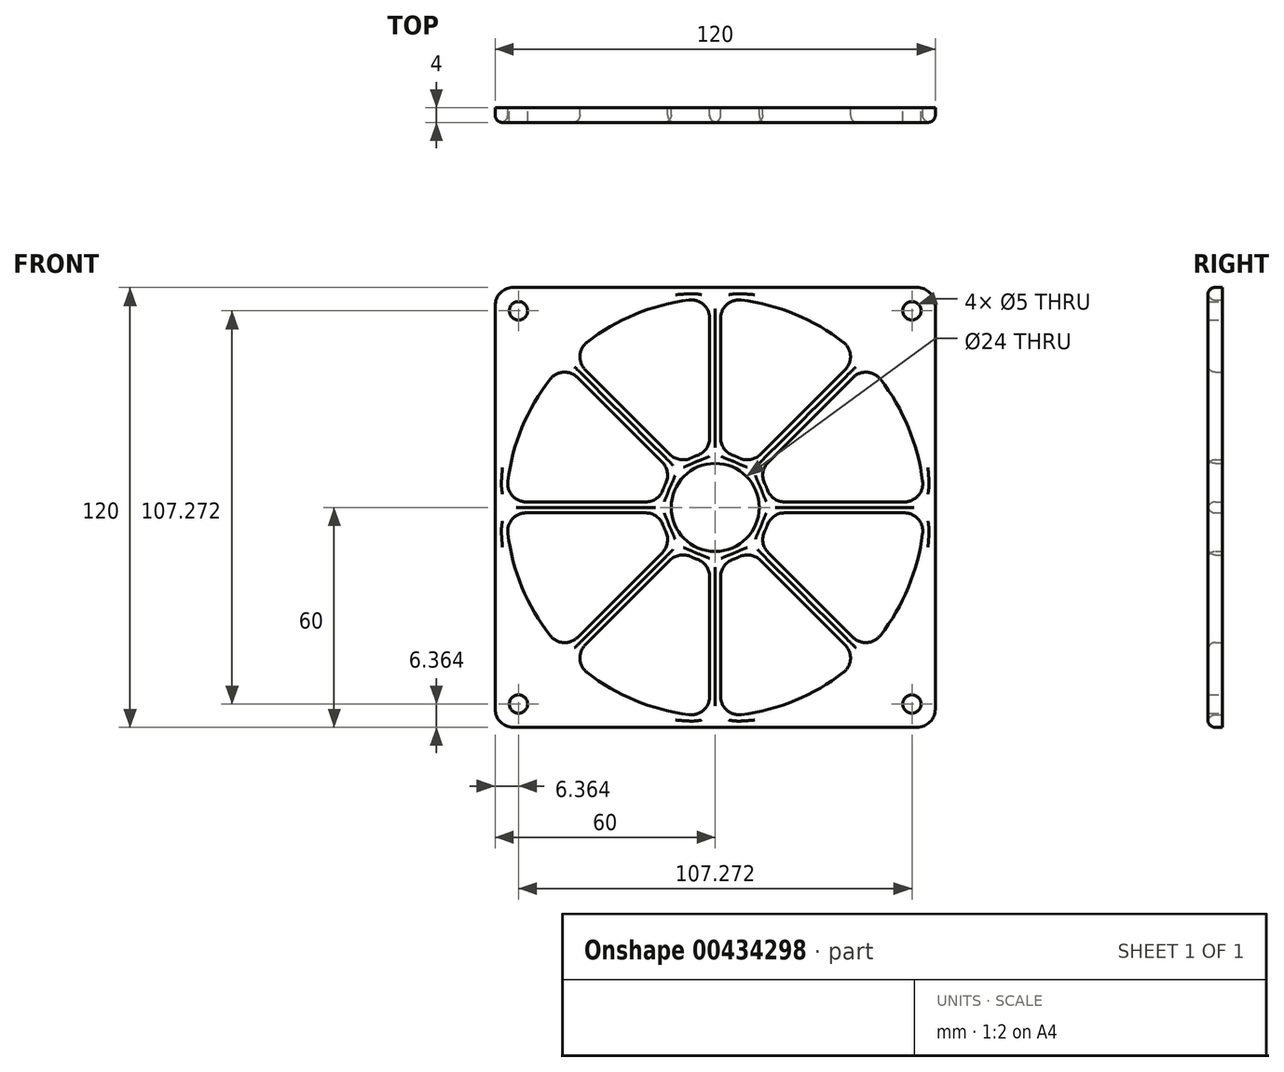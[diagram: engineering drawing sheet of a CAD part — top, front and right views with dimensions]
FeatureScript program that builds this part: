
annotation { "Feature Type Name" : "Feature", "Feature Type Description" : "" }
export const myFeature = defineFeature(function(context is Context, id is Id, definition is map)
    precondition{}
    {
        {
            var Q0;
            Q0=qCreatedBy(makeId("Front.planeOp"),FACE);
            var sketch = newSketch(context, id + "F0", { "sketchPlane" : qUnion([Q0])});
            skLineSegment(sketch, "E0.bottom", {"start": v(-60, 60) * mm, "end": v(60, 60) * mm});
            skLineSegment(sketch, "E0.top", {"start": v(-60, -60) * mm, "end": v(60, -60) * mm});
            skLineSegment(sketch, "E0.left", {"start": v(-60, 60) * mm, "end": v(-60, -60) * mm});
            skLineSegment(sketch, "E0.right", {"start": v(60, 60) * mm, "end": v(60, -60) * mm});
            skCircle(sketch, "E1", {"center": v(0, 0) * mm, "radius": 57 * mm});
            skCircle(sketch, "E2", {"center": v(0, 0) * mm, "radius": 15 * mm});
            skLineSegment(sketch, "E3", {"start": v(0, 57) * mm, "end": v(0, 15) * mm});
            skLineSegment(sketch, "E4", {"start": v(15, 0) * mm, "end": v(57, 0) * mm});
            skLineSegment(sketch, "E5", {"start": v(0, -15) * mm, "end": v(0, -57) * mm});
            skLineSegment(sketch, "E6", {"start": v(-15, 0) * mm, "end": v(-57, 0) * mm});
            skLineSegment(sketch, "E7", {"start": v(-1.5, -14.92) * mm, "end": v(-1.5, -56.98) * mm});
            skLineSegment(sketch, "E8", {"start": v(1.5, -14.92) * mm, "end": v(1.5, -56.98) * mm});
            skLineSegment(sketch, "E9", {"start": v(9.5, -11.61) * mm, "end": v(39.23, -41.35) * mm});
            skLineSegment(sketch, "E10", {"start": v(11.61, -9.5) * mm, "end": v(41.35, -39.23) * mm});
            skLineSegment(sketch, "E11", {"start": v(14.92, -1.5) * mm, "end": v(56.98, -1.5) * mm});
            skLineSegment(sketch, "E12", {"start": v(14.92, 1.5) * mm, "end": v(56.98, 1.5) * mm});
            skLineSegment(sketch, "E13", {"start": v(11.61, 9.5) * mm, "end": v(41.35, 39.23) * mm});
            skLineSegment(sketch, "E14", {"start": v(9.5, 11.61) * mm, "end": v(39.23, 41.35) * mm});
            skLineSegment(sketch, "E15", {"start": v(1.5, 14.93) * mm, "end": v(1.5, 56.98) * mm});
            skLineSegment(sketch, "E16", {"start": v(-1.5, 56.98) * mm, "end": v(-1.5, 14.92) * mm});
            skLineSegment(sketch, "E17", {"start": v(-9.5, 11.61) * mm, "end": v(-39.23, 41.35) * mm});
            skLineSegment(sketch, "E18", {"start": v(-11.61, 9.5) * mm, "end": v(-41.35, 39.23) * mm});
            skLineSegment(sketch, "E19", {"start": v(-14.92, 1.5) * mm, "end": v(-56.98, 1.5) * mm});
            skLineSegment(sketch, "E20", {"start": v(-14.93, -1.5) * mm, "end": v(-56.98, -1.5) * mm});
            skLineSegment(sketch, "E21", {"start": v(-9.5, -11.61) * mm, "end": v(-39.23, -41.35) * mm});
            skLineSegment(sketch, "E22", {"start": v(-11.61, -9.5) * mm, "end": v(-41.35, -39.23) * mm});
            skPoint(sketch, "E23", {"position": v(40.3, -40.3) * mm});
            skPoint(sketch, "E24", {"position": v(40.3, 40.3) * mm});
            skPoint(sketch, "E25", {"position": v(-40.3, 40.3) * mm});
            skPoint(sketch, "E26", {"position": v(-10.6, 10.6) * mm});
            skPoint(sketch, "E27", {"position": v(10.6, 10.6) * mm});
            skPoint(sketch, "E28", {"position": v(-10.6, -10.6) * mm});
            skPoint(sketch, "E29", {"position": v(10.6, -10.6) * mm});
            skPoint(sketch, "E30", {"position": v(-40.3, -40.3) * mm});
            skCircle(sketch, "E31", {"center": v(-53.64, -53.64) * mm, "radius": 2.5 * mm});
            skCircle(sketch, "E32", {"center": v(53.64, -53.64) * mm, "radius": 2.5 * mm});
            skCircle(sketch, "E33", {"center": v(53.64, 53.64) * mm, "radius": 2.5 * mm});
            skCircle(sketch, "E34", {"center": v(-53.64, 53.64) * mm, "radius": 2.5 * mm});
            skCircle(sketch, "E35", {"center": v(0, 0) * mm, "radius": 12 * mm});
            skSolve(sketch);
        }
        {
            var Q0;
            Q0=makeQuery(id+"F0.imprint","IMPRINT",FACE,{"disambiguationData":[TD([[makeQuery(id+"F0.imprint","IMPRINT",EDGE,{"derivedFrom":sQuery(id+"F0.wireOp",EDGE,"E0.bottom")}),-1.0]])]});
            var Q1;
            {var subQ0=sQuery(id+"F0.wireOp",EDGE,"E17");Q1=makeQuery(id+"F0.imprint","IMPRINT",FACE,{"disambiguationData":[TD([[makeQuery(id+"F0.imprint","IMPRINT",EDGE,{"derivedFrom":subQ0}),1.0]])]});}
            var Q2;
            {var subQ0=sQuery(id+"F0.wireOp",EDGE,"E13");Q2=makeQuery(id+"F0.imprint","IMPRINT",FACE,{"disambiguationData":[TD([[makeQuery(id+"F0.imprint","IMPRINT",EDGE,{"derivedFrom":subQ0}),1.0]])]});}
            var Q3;
            {var subQ0=sQuery(id+"F0.wireOp",EDGE,"E3");Q3=makeQuery(id+"F0.imprint","IMPRINT",FACE,{"disambiguationData":[TD([[makeQuery(id+"F0.imprint","IMPRINT",EDGE,{"derivedFrom":subQ0}),-1.0]])]});}
            var Q4;
            {var subQ0=sQuery(id+"F0.wireOp",EDGE,"E3");Q4=makeQuery(id+"F0.imprint","IMPRINT",FACE,{"disambiguationData":[TD([[makeQuery(id+"F0.imprint","IMPRINT",EDGE,{"derivedFrom":subQ0}),1.0]])]});}
            var Q5;
            {var subQ0=sQuery(id+"F0.wireOp",EDGE,"E2");var subQ8=makeQuery(id+"F0.imprint","INTERSECT",VERTEX,{"derivedFrom":[subQ0,sQuery(id+"F0.wireOp",EDGE,"E4")]});Q5=makeQuery(id+"F0.imprint","IMPRINT",FACE,{"disambiguationData":[TD([[makeQuery(id+"F0.imprint","IMPRINT",EDGE,{"disambiguationData":[TD([[subQ8,-1.0]])],"derivedFrom":subQ0}),1.0]])]});}
            var Q6;
            {var subQ0=sQuery(id+"F0.wireOp",EDGE,"E4");Q6=makeQuery(id+"F0.imprint","IMPRINT",FACE,{"disambiguationData":[TD([[makeQuery(id+"F0.imprint","IMPRINT",EDGE,{"derivedFrom":subQ0}),1.0]])]});}
            var Q7;
            {var subQ0=sQuery(id+"F0.wireOp",EDGE,"E4");Q7=makeQuery(id+"F0.imprint","IMPRINT",FACE,{"disambiguationData":[TD([[makeQuery(id+"F0.imprint","IMPRINT",EDGE,{"derivedFrom":subQ0}),-1.0]])]});}
            var Q8;
            {var subQ0=sQuery(id+"F0.wireOp",EDGE,"E9");Q8=makeQuery(id+"F0.imprint","IMPRINT",FACE,{"disambiguationData":[TD([[makeQuery(id+"F0.imprint","IMPRINT",EDGE,{"derivedFrom":subQ0}),1.0]])]});}
            var Q9;
            {var subQ0=sQuery(id+"F0.wireOp",EDGE,"E5");Q9=makeQuery(id+"F0.imprint","IMPRINT",FACE,{"disambiguationData":[TD([[makeQuery(id+"F0.imprint","IMPRINT",EDGE,{"derivedFrom":subQ0}),1.0]])]});}
            var Q10;
            {var subQ0=sQuery(id+"F0.wireOp",EDGE,"E5");Q10=makeQuery(id+"F0.imprint","IMPRINT",FACE,{"disambiguationData":[TD([[makeQuery(id+"F0.imprint","IMPRINT",EDGE,{"derivedFrom":subQ0}),-1.0]])]});}
            var Q11;
            {var subQ0=sQuery(id+"F0.wireOp",EDGE,"E21");Q11=makeQuery(id+"F0.imprint","IMPRINT",FACE,{"disambiguationData":[TD([[makeQuery(id+"F0.imprint","IMPRINT",EDGE,{"derivedFrom":subQ0}),-1.0]])]});}
            var Q12;
            {var subQ0=sQuery(id+"F0.wireOp",EDGE,"E6");Q12=makeQuery(id+"F0.imprint","IMPRINT",FACE,{"disambiguationData":[TD([[makeQuery(id+"F0.imprint","IMPRINT",EDGE,{"derivedFrom":subQ0}),1.0]])]});}
            var Q13;
            {var subQ0=sQuery(id+"F0.wireOp",EDGE,"E6");Q13=makeQuery(id+"F0.imprint","IMPRINT",FACE,{"disambiguationData":[TD([[makeQuery(id+"F0.imprint","IMPRINT",EDGE,{"derivedFrom":subQ0}),-1.0]])]});}
            extrude(context, id + "F1", {"entities" : qUnion([Q0, Q1, Q2, Q3, Q4, Q5, Q6, Q7, Q8, Q9, Q10, Q11, Q12, Q13]), "depth" : 4 * mm});
        }
        {
            var Q0;
            Q0=makeQuery(id+"F1.opExtrude","SWEPT_EDGE",EDGE,{"disambiguationData":[OSD([sQuery(id+"F0.wireOp",EDGE,"E0.bottom"),sQuery(id+"F0.wireOp",EDGE,"E0.left")])]});
            var Q1;
            Q1=makeQuery(id+"F1.opExtrude","SWEPT_EDGE",EDGE,{"disambiguationData":[OSD([sQuery(id+"F0.wireOp",EDGE,"E0.bottom"),sQuery(id+"F0.wireOp",EDGE,"E0.right")])]});
            var Q2;
            Q2=makeQuery(id+"F1.opExtrude","SWEPT_EDGE",EDGE,{"disambiguationData":[OSD([sQuery(id+"F0.wireOp",EDGE,"E0.top"),sQuery(id+"F0.wireOp",EDGE,"E0.right")])]});
            var Q3;
            Q3=makeQuery(id+"F1.opExtrude","SWEPT_EDGE",EDGE,{"disambiguationData":[OSD([sQuery(id+"F0.wireOp",EDGE,"E0.top"),sQuery(id+"F0.wireOp",EDGE,"E0.left")])]});
            var Q4;
            Q4=makeQuery(id+"F1.opExtrude","SWEPT_EDGE",EDGE,{"disambiguationData":[OSD([sQuery(id+"F0.wireOp",EDGE,"E2"),sQuery(id+"F0.wireOp",EDGE,"E19")])]});
            var Q5;
            Q5=makeQuery(id+"F1.opExtrude","SWEPT_EDGE",EDGE,{"disambiguationData":[OSD([sQuery(id+"F0.wireOp",EDGE,"E2"),sQuery(id+"F0.wireOp",EDGE,"E18")])]});
            var Q6;
            Q6=makeQuery(id+"F1.opExtrude","SWEPT_EDGE",EDGE,{"disambiguationData":[OSD([sQuery(id+"F0.wireOp",EDGE,"E2"),sQuery(id+"F0.wireOp",EDGE,"E17")])]});
            var Q7;
            Q7=makeQuery(id+"F1.opExtrude","SWEPT_EDGE",EDGE,{"disambiguationData":[OSD([sQuery(id+"F0.wireOp",EDGE,"E2"),sQuery(id+"F0.wireOp",EDGE,"E16")])]});
            var Q8;
            Q8=makeQuery(id+"F1.opExtrude","SWEPT_EDGE",EDGE,{"disambiguationData":[OSD([sQuery(id+"F0.wireOp",EDGE,"E1"),sQuery(id+"F0.wireOp",EDGE,"E17")])]});
            var Q9;
            Q9=makeQuery(id+"F1.opExtrude","SWEPT_EDGE",EDGE,{"disambiguationData":[OSD([sQuery(id+"F0.wireOp",EDGE,"E1"),sQuery(id+"F0.wireOp",EDGE,"E18")])]});
            var Q10;
            Q10=makeQuery(id+"F1.opExtrude","SWEPT_EDGE",EDGE,{"disambiguationData":[OSD([sQuery(id+"F0.wireOp",EDGE,"E1"),sQuery(id+"F0.wireOp",EDGE,"E19")])]});
            var Q11;
            Q11=makeQuery(id+"F1.opExtrude","SWEPT_EDGE",EDGE,{"disambiguationData":[OSD([sQuery(id+"F0.wireOp",EDGE,"E1"),sQuery(id+"F0.wireOp",EDGE,"E20")])]});
            var Q12;
            Q12=makeQuery(id+"F1.opExtrude","SWEPT_EDGE",EDGE,{"disambiguationData":[OSD([sQuery(id+"F0.wireOp",EDGE,"E1"),sQuery(id+"F0.wireOp",EDGE,"E22")])]});
            var Q13;
            Q13=makeQuery(id+"F1.opExtrude","SWEPT_EDGE",EDGE,{"disambiguationData":[OSD([sQuery(id+"F0.wireOp",EDGE,"E2"),sQuery(id+"F0.wireOp",EDGE,"E20")])]});
            var Q14;
            Q14=makeQuery(id+"F1.opExtrude","SWEPT_EDGE",EDGE,{"disambiguationData":[OSD([sQuery(id+"F0.wireOp",EDGE,"E2"),sQuery(id+"F0.wireOp",EDGE,"E22")])]});
            var Q15;
            Q15=makeQuery(id+"F1.opExtrude","SWEPT_EDGE",EDGE,{"disambiguationData":[OSD([sQuery(id+"F0.wireOp",EDGE,"E2"),sQuery(id+"F0.wireOp",EDGE,"E21")])]});
            var Q16;
            Q16=makeQuery(id+"F1.opExtrude","SWEPT_EDGE",EDGE,{"disambiguationData":[OSD([sQuery(id+"F0.wireOp",EDGE,"E1"),sQuery(id+"F0.wireOp",EDGE,"E21")])]});
            var Q17;
            Q17=makeQuery(id+"F1.opExtrude","SWEPT_EDGE",EDGE,{"disambiguationData":[OSD([sQuery(id+"F0.wireOp",EDGE,"E1"),sQuery(id+"F0.wireOp",EDGE,"E7")])]});
            var Q18;
            Q18=makeQuery(id+"F1.opExtrude","SWEPT_EDGE",EDGE,{"disambiguationData":[OSD([sQuery(id+"F0.wireOp",EDGE,"E2"),sQuery(id+"F0.wireOp",EDGE,"E7")])]});
            var Q19;
            Q19=makeQuery(id+"F1.opExtrude","SWEPT_EDGE",EDGE,{"disambiguationData":[OSD([sQuery(id+"F0.wireOp",EDGE,"E2"),sQuery(id+"F0.wireOp",EDGE,"E8")])]});
            var Q20;
            Q20=makeQuery(id+"F1.opExtrude","SWEPT_EDGE",EDGE,{"disambiguationData":[OSD([sQuery(id+"F0.wireOp",EDGE,"E1"),sQuery(id+"F0.wireOp",EDGE,"E8")])]});
            var Q21;
            Q21=makeQuery(id+"F1.opExtrude","SWEPT_EDGE",EDGE,{"disambiguationData":[OSD([sQuery(id+"F0.wireOp",EDGE,"E1"),sQuery(id+"F0.wireOp",EDGE,"E9")])]});
            var Q22;
            Q22=makeQuery(id+"F1.opExtrude","SWEPT_EDGE",EDGE,{"disambiguationData":[OSD([sQuery(id+"F0.wireOp",EDGE,"E2"),sQuery(id+"F0.wireOp",EDGE,"E9")])]});
            var Q23;
            Q23=makeQuery(id+"F1.opExtrude","SWEPT_EDGE",EDGE,{"disambiguationData":[OSD([sQuery(id+"F0.wireOp",EDGE,"E2"),sQuery(id+"F0.wireOp",EDGE,"E10")])]});
            var Q24;
            Q24=makeQuery(id+"F1.opExtrude","SWEPT_EDGE",EDGE,{"disambiguationData":[OSD([sQuery(id+"F0.wireOp",EDGE,"E1"),sQuery(id+"F0.wireOp",EDGE,"E10")])]});
            var Q25;
            Q25=makeQuery(id+"F1.opExtrude","SWEPT_EDGE",EDGE,{"disambiguationData":[OSD([sQuery(id+"F0.wireOp",EDGE,"E1"),sQuery(id+"F0.wireOp",EDGE,"E11")])]});
            var Q26;
            Q26=makeQuery(id+"F1.opExtrude","SWEPT_EDGE",EDGE,{"disambiguationData":[OSD([sQuery(id+"F0.wireOp",EDGE,"E2"),sQuery(id+"F0.wireOp",EDGE,"E11")])]});
            var Q27;
            Q27=makeQuery(id+"F1.opExtrude","SWEPT_EDGE",EDGE,{"disambiguationData":[OSD([sQuery(id+"F0.wireOp",EDGE,"E2"),sQuery(id+"F0.wireOp",EDGE,"E12")])]});
            var Q28;
            Q28=makeQuery(id+"F1.opExtrude","SWEPT_EDGE",EDGE,{"disambiguationData":[OSD([sQuery(id+"F0.wireOp",EDGE,"E1"),sQuery(id+"F0.wireOp",EDGE,"E12")])]});
            var Q29;
            Q29=makeQuery(id+"F1.opExtrude","SWEPT_EDGE",EDGE,{"disambiguationData":[OSD([sQuery(id+"F0.wireOp",EDGE,"E1"),sQuery(id+"F0.wireOp",EDGE,"E13")])]});
            var Q30;
            Q30=makeQuery(id+"F1.opExtrude","SWEPT_EDGE",EDGE,{"disambiguationData":[OSD([sQuery(id+"F0.wireOp",EDGE,"E2"),sQuery(id+"F0.wireOp",EDGE,"E13")])]});
            var Q31;
            Q31=makeQuery(id+"F1.opExtrude","SWEPT_EDGE",EDGE,{"disambiguationData":[OSD([sQuery(id+"F0.wireOp",EDGE,"E2"),sQuery(id+"F0.wireOp",EDGE,"E14")])]});
            var Q32;
            Q32=makeQuery(id+"F1.opExtrude","SWEPT_EDGE",EDGE,{"disambiguationData":[OSD([sQuery(id+"F0.wireOp",EDGE,"E2"),sQuery(id+"F0.wireOp",EDGE,"E15")])]});
            var Q33;
            Q33=makeQuery(id+"F1.opExtrude","SWEPT_EDGE",EDGE,{"disambiguationData":[OSD([sQuery(id+"F0.wireOp",EDGE,"E1"),sQuery(id+"F0.wireOp",EDGE,"E14")])]});
            var Q34;
            Q34=makeQuery(id+"F1.opExtrude","SWEPT_EDGE",EDGE,{"disambiguationData":[OSD([sQuery(id+"F0.wireOp",EDGE,"E1"),sQuery(id+"F0.wireOp",EDGE,"E15")])]});
            var Q35;
            Q35=makeQuery(id+"F1.opExtrude","SWEPT_EDGE",EDGE,{"disambiguationData":[OSD([sQuery(id+"F0.wireOp",EDGE,"E1"),sQuery(id+"F0.wireOp",EDGE,"E16")])]});
            fillet(context, id + "F2", {"entities" : qUnion([Q0, Q1, Q2, Q3, Q4, Q5, Q6, Q7, Q8, Q9, Q10, Q11, Q12, Q13, Q14, Q15, Q16, Q17, Q18, Q19, Q20, Q21, Q22, Q23, Q24, Q25, Q26, Q27, Q28, Q29, Q30, Q31, Q32, Q33, Q34, Q35]), "radius" : 5 * mm, "tangentPropagation" : true, "allowEdgeOverflow" : false});
        }
        {
            var Q0;
            Q0=makeQuery(id+"F1.opExtrude","CAP_EDGE",EDGE,{"disambiguationData":[OSD([sQuery(id+"F0.wireOp",EDGE,"E35")])],"isStart":false});
            var Q1;
            {var subQ0=sQuery(id+"F0.wireOp",EDGE,"E1");Q1=makeQuery(id+"F1.opExtrude","CAP_EDGE",EDGE,{"disambiguationData":[OSD([subQ0]),TDD([makeQuery(id+"F0.imprint","IMPRINT",EDGE,{"disambiguationData":[TD([[makeQuery(id+"F0.imprint","INTERSECT",VERTEX,{"derivedFrom":[subQ0,sQuery(id+"F0.wireOp",EDGE,"E8")]}),-1.0]])],"derivedFrom":subQ0})])],"isStart":false});}
            var Q2;
            {var subQ0=sQuery(id+"F0.wireOp",EDGE,"E1");Q2=makeQuery(id+"F1.opExtrude","CAP_EDGE",EDGE,{"disambiguationData":[OSD([subQ0]),TDD([makeQuery(id+"F0.imprint","IMPRINT",EDGE,{"disambiguationData":[TD([[makeQuery(id+"F0.imprint","INTERSECT",VERTEX,{"derivedFrom":[subQ0,sQuery(id+"F0.wireOp",EDGE,"E10")]}),-1.0]])],"derivedFrom":subQ0})])],"isStart":false});}
            var Q3;
            {var subQ0=sQuery(id+"F0.wireOp",EDGE,"E1");Q3=makeQuery(id+"F1.opExtrude","CAP_EDGE",EDGE,{"disambiguationData":[OSD([subQ0]),TDD([makeQuery(id+"F0.imprint","IMPRINT",EDGE,{"disambiguationData":[TD([[makeQuery(id+"F0.imprint","INTERSECT",VERTEX,{"derivedFrom":[subQ0,sQuery(id+"F0.wireOp",EDGE,"E12")]}),-1.0]])],"derivedFrom":subQ0})])],"isStart":false});}
            var Q4;
            {var subQ0=sQuery(id+"F0.wireOp",EDGE,"E1");Q4=makeQuery(id+"F1.opExtrude","CAP_EDGE",EDGE,{"disambiguationData":[OSD([subQ0]),TDD([makeQuery(id+"F0.imprint","IMPRINT",EDGE,{"disambiguationData":[TD([[makeQuery(id+"F0.imprint","INTERSECT",VERTEX,{"derivedFrom":[subQ0,sQuery(id+"F0.wireOp",EDGE,"E14")]}),-1.0]])],"derivedFrom":subQ0})])],"isStart":false});}
            var Q5;
            {var subQ0=sQuery(id+"F0.wireOp",EDGE,"E1");Q5=makeQuery(id+"F1.opExtrude","CAP_EDGE",EDGE,{"disambiguationData":[OSD([subQ0]),TDD([makeQuery(id+"F0.imprint","IMPRINT",EDGE,{"disambiguationData":[TD([[makeQuery(id+"F0.imprint","INTERSECT",VERTEX,{"derivedFrom":[subQ0,sQuery(id+"F0.wireOp",EDGE,"E16")]}),-1.0]])],"derivedFrom":subQ0})])],"isStart":false});}
            var Q6;
            {var subQ0=sQuery(id+"F0.wireOp",EDGE,"E1");Q6=makeQuery(id+"F1.opExtrude","CAP_EDGE",EDGE,{"disambiguationData":[OSD([subQ0]),TDD([makeQuery(id+"F0.imprint","IMPRINT",EDGE,{"disambiguationData":[TD([[makeQuery(id+"F0.imprint","INTERSECT",VERTEX,{"derivedFrom":[subQ0,sQuery(id+"F0.wireOp",EDGE,"E18")]}),-1.0]])],"derivedFrom":subQ0})])],"isStart":false});}
            var Q7;
            {var subQ0=sQuery(id+"F0.wireOp",EDGE,"E1");Q7=makeQuery(id+"F1.opExtrude","CAP_EDGE",EDGE,{"disambiguationData":[OSD([subQ0]),TDD([makeQuery(id+"F0.imprint","IMPRINT",EDGE,{"disambiguationData":[TD([[makeQuery(id+"F0.imprint","INTERSECT",VERTEX,{"derivedFrom":[subQ0,sQuery(id+"F0.wireOp",EDGE,"E20")]}),-1.0]])],"derivedFrom":subQ0})])],"isStart":false});}
            var Q8;
            {var subQ0=sQuery(id+"F0.wireOp",EDGE,"E1");Q8=makeQuery(id+"F1.opExtrude","CAP_EDGE",EDGE,{"disambiguationData":[OSD([subQ0]),TDD([makeQuery(id+"F0.imprint","IMPRINT",EDGE,{"disambiguationData":[TD([[makeQuery(id+"F0.imprint","INTERSECT",VERTEX,{"derivedFrom":[subQ0,sQuery(id+"F0.wireOp",EDGE,"E7")]}),1.0]])],"derivedFrom":subQ0})])],"isStart":false});}
            var Q9;
            Q9=makeQuery(id+"F1.opExtrude","CAP_EDGE",EDGE,{"disambiguationData":[OSD([sQuery(id+"F0.wireOp",EDGE,"E0.bottom")])],"isStart":false});
            fillet(context, id + "F3", {"entities" : qUnion([Q0, Q1, Q2, Q3, Q4, Q5, Q6, Q7, Q8, Q9]), "radius" : 2 * mm, "tangentPropagation" : true, "allowEdgeOverflow" : false});
        }
    });
